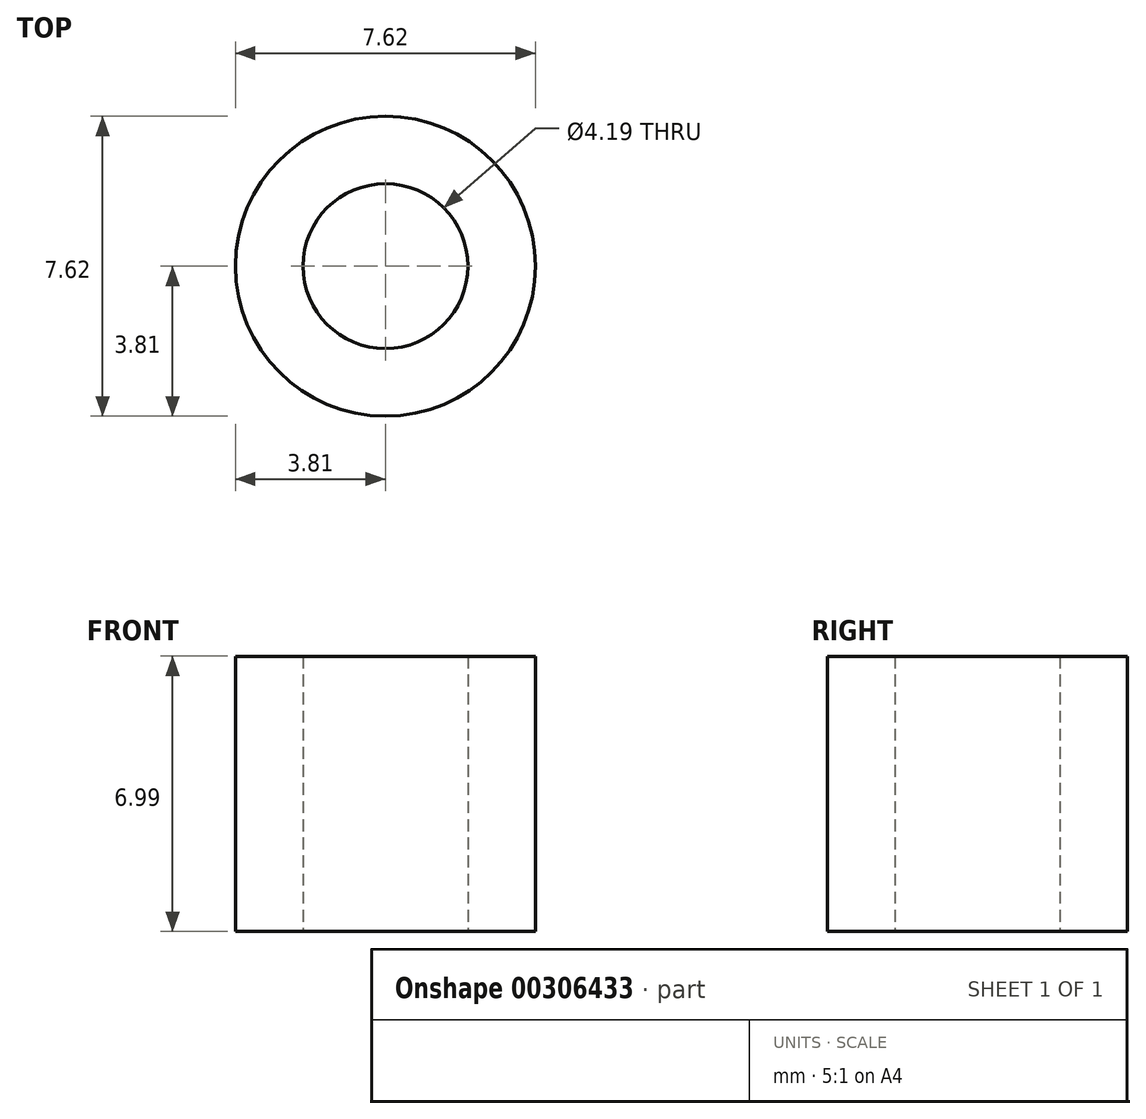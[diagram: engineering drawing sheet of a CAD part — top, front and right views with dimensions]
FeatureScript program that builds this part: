
annotation { "Feature Type Name" : "Feature", "Feature Type Description" : "" }
export const myFeature = defineFeature(function(context is Context, id is Id, definition is map)
    precondition{}
    {
        {
            var Q0;
            Q0=qCreatedBy(makeId("Top.planeOp"),FACE);
            var sketch = newSketch(context, id + "F0", { "sketchPlane" : qUnion([Q0])});
            skCircle(sketch, "E0", {"center": v(0, 0) * mm, "radius": 2.1 * mm});
            skCircle(sketch, "E1", {"center": v(0, 0) * mm, "radius": 3.81 * mm});
            skSolve(sketch);
        }
        {
            var Q0;
            Q0 = qSketchRegion(id + "F0", true);
            extrude(context, id + "F1", {"entities" : qUnion([Q0]), "depth" : 7 * mm});
        }
    });
